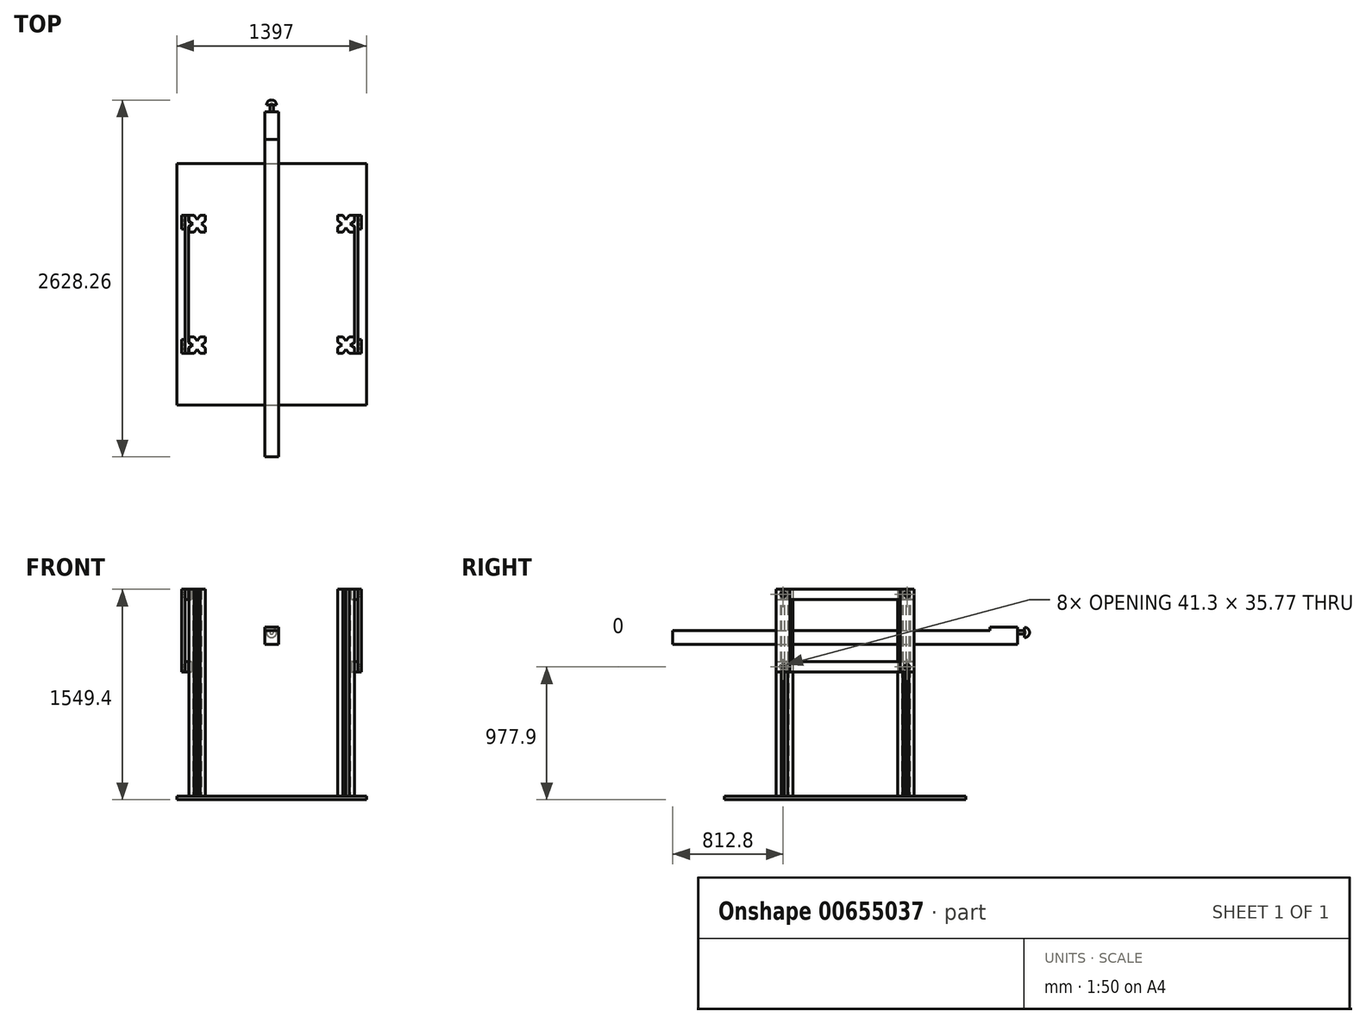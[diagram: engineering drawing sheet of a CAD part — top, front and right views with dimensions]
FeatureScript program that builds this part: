
annotation { "Feature Type Name" : "Feature", "Feature Type Description" : "" }
export const myFeature = defineFeature(function(context is Context, id is Id, definition is map)
    precondition{}
    {
        {
            var Q0;
            Q0=qCreatedBy(makeId("Top.planeOp"),FACE);
            var sketch = newSketch(context, id + "F0", { "sketchPlane" : qUnion([Q0])});
            skLineSegment(sketch, "E0.bottom", {"start": v(-698.5, 889) * mm, "end": v(698.5, 889) * mm});
            skLineSegment(sketch, "E0.top", {"start": v(-698.5, -889) * mm, "end": v(698.5, -889) * mm});
            skLineSegment(sketch, "E0.left", {"start": v(-698.5, 889) * mm, "end": v(-698.5, -889) * mm});
            skLineSegment(sketch, "E0.right", {"start": v(698.5, 889) * mm, "end": v(698.5, -889) * mm});
            skSolve(sketch);
        }
        {
            var Q0;
            Q0 = qSketchRegion(id + "F0", true);
            extrude(context, id + "F1", {"entities" : qUnion([Q0]), "depth" : 25.4 * mm, "offsetDistance" : 25.4 * mm});
        }
        {
            var Q0;
            Q0=makeQuery(id+"F1.opExtrude","CAP_FACE",FACE,{"disambiguationData":[OSD([sQuery(id+"F0.wireOp",EDGE,"E0.bottom"),sQuery(id+"F0.wireOp",EDGE,"E0.top"),sQuery(id+"F0.wireOp",EDGE,"E0.left"),sQuery(id+"F0.wireOp",EDGE,"E0.right")])],"isStart":false});
            var sketch = newSketch(context, id + "F2", { "sketchPlane" : qUnion([Q0])});
            skLineSegment(sketch, "E1", {"start": v(-609.6, 508) * mm, "end": v(-571.5, 508) * mm});
            skLineSegment(sketch, "E2", {"start": v(-571.5, 508) * mm, "end": v(-548.3, 477.77) * mm});
            skLineSegment(sketch, "E3", {"start": v(-548.3, 477.77) * mm, "end": v(-525.11, 508) * mm});
            skLineSegment(sketch, "E4", {"start": v(-525.11, 508) * mm, "end": v(-487.01, 508) * mm});
            skLineSegment(sketch, "E5", {"start": v(-487.01, 508) * mm, "end": v(-487.01, 469.9) * mm});
            skLineSegment(sketch, "E6", {"start": v(-487.01, 469.9) * mm, "end": v(-517.24, 446.7) * mm});
            skLineSegment(sketch, "E7", {"start": v(-517.24, 446.7) * mm, "end": v(-487.01, 423.51) * mm});
            skLineSegment(sketch, "E8", {"start": v(-487.01, 423.51) * mm, "end": v(-487.01, 385.41) * mm});
            skLineSegment(sketch, "E9", {"start": v(-487.01, 385.41) * mm, "end": v(-525.11, 385.41) * mm});
            skLineSegment(sketch, "E10", {"start": v(-525.11, 385.41) * mm, "end": v(-548.3, 415.64) * mm});
            skLineSegment(sketch, "E11", {"start": v(-548.3, 415.64) * mm, "end": v(-571.5, 385.41) * mm});
            skLineSegment(sketch, "E12", {"start": v(-571.5, 385.41) * mm, "end": v(-609.6, 385.41) * mm});
            skLineSegment(sketch, "E13", {"start": v(-609.6, 385.41) * mm, "end": v(-609.6, 423.51) * mm});
            skLineSegment(sketch, "E14", {"start": v(-609.6, 423.51) * mm, "end": v(-579.37, 446.7) * mm});
            skLineSegment(sketch, "E15", {"start": v(-579.37, 446.7) * mm, "end": v(-609.6, 469.9) * mm});
            skLineSegment(sketch, "E16", {"start": v(-609.6, 469.9) * mm, "end": v(-609.6, 508) * mm});
            skLineSegment(sketch, "E17.MirrorCS", {"start": v(-571.5, -508) * mm, "end": v(-548.3, -477.77) * mm});
            skLineSegment(sketch, "E18.MirrorCS", {"start": v(-548.3, -477.77) * mm, "end": v(-525.11, -508) * mm});
            skLineSegment(sketch, "E19.MirrorCS", {"start": v(-525.11, -508) * mm, "end": v(-487.01, -508) * mm});
            skLineSegment(sketch, "E20.MirrorCS", {"start": v(-487.01, -508) * mm, "end": v(-487.01, -469.9) * mm});
            skLineSegment(sketch, "E21.MirrorCS", {"start": v(-487.01, -469.9) * mm, "end": v(-517.24, -446.7) * mm});
            skLineSegment(sketch, "E22.MirrorCS", {"start": v(-517.24, -446.7) * mm, "end": v(-487.01, -423.51) * mm});
            skLineSegment(sketch, "E23.MirrorCS", {"start": v(-487.01, -423.51) * mm, "end": v(-487.01, -385.41) * mm});
            skLineSegment(sketch, "E24.MirrorCS", {"start": v(-487.01, -385.41) * mm, "end": v(-525.11, -385.41) * mm});
            skLineSegment(sketch, "E25.MirrorCS", {"start": v(-609.6, -508) * mm, "end": v(-571.5, -508) * mm});
            skLineSegment(sketch, "E26.MirrorCS", {"start": v(-571.5, -385.41) * mm, "end": v(-609.6, -385.41) * mm});
            skLineSegment(sketch, "E27.MirrorCS", {"start": v(-609.6, -385.41) * mm, "end": v(-609.6, -423.51) * mm});
            skLineSegment(sketch, "E28.MirrorCS", {"start": v(-609.6, -423.51) * mm, "end": v(-579.37, -446.7) * mm});
            skLineSegment(sketch, "E29.MirrorCS", {"start": v(-548.3, -415.64) * mm, "end": v(-571.5, -385.41) * mm});
            skLineSegment(sketch, "E30.MirrorCS", {"start": v(-525.11, -385.41) * mm, "end": v(-548.3, -415.64) * mm});
            skLineSegment(sketch, "E31.MirrorCS", {"start": v(-609.6, -469.9) * mm, "end": v(-609.6, -508) * mm});
            skLineSegment(sketch, "E32.MirrorCS", {"start": v(-579.37, -446.7) * mm, "end": v(-609.6, -469.9) * mm});
            skLineSegment(sketch, "E33.MirrorCS", {"start": v(525.11, -385.41) * mm, "end": v(548.3, -415.64) * mm});
            skLineSegment(sketch, "E34.MirrorCS", {"start": v(571.5, 385.41) * mm, "end": v(609.6, 385.41) * mm});
            skLineSegment(sketch, "E35.MirrorCS", {"start": v(525.11, -508) * mm, "end": v(487.01, -508) * mm});
            skLineSegment(sketch, "E36.MirrorCS", {"start": v(571.5, 508) * mm, "end": v(548.3, 477.77) * mm});
            skLineSegment(sketch, "E37.MirrorCS", {"start": v(517.24, 446.7) * mm, "end": v(487.01, 423.51) * mm});
            skLineSegment(sketch, "E38.MirrorCS", {"start": v(609.6, -385.41) * mm, "end": v(609.6, -423.51) * mm});
            skLineSegment(sketch, "E39.MirrorCS", {"start": v(609.6, 469.9) * mm, "end": v(609.6, 508) * mm});
            skLineSegment(sketch, "E40.MirrorCS", {"start": v(609.6, -508) * mm, "end": v(571.5, -508) * mm});
            skLineSegment(sketch, "E41.MirrorCS", {"start": v(579.37, -446.7) * mm, "end": v(609.6, -469.9) * mm});
            skLineSegment(sketch, "E42.MirrorCS", {"start": v(517.24, -446.7) * mm, "end": v(487.01, -423.51) * mm});
            skLineSegment(sketch, "E43.MirrorCS", {"start": v(487.01, 508) * mm, "end": v(487.01, 469.9) * mm});
            skLineSegment(sketch, "E44.MirrorCS", {"start": v(609.6, -469.9) * mm, "end": v(609.6, -508) * mm});
            skLineSegment(sketch, "E45.MirrorCS", {"start": v(487.01, -423.51) * mm, "end": v(487.01, -385.41) * mm});
            skLineSegment(sketch, "E46.MirrorCS", {"start": v(487.01, -469.9) * mm, "end": v(517.24, -446.7) * mm});
            skLineSegment(sketch, "E47.MirrorCS", {"start": v(487.01, 385.41) * mm, "end": v(525.11, 385.41) * mm});
            skLineSegment(sketch, "E48.MirrorCS", {"start": v(609.6, -423.51) * mm, "end": v(579.37, -446.7) * mm});
            skLineSegment(sketch, "E49.MirrorCS", {"start": v(548.3, 477.77) * mm, "end": v(525.11, 508) * mm});
            skLineSegment(sketch, "E50.MirrorCS", {"start": v(487.01, -385.41) * mm, "end": v(525.11, -385.41) * mm});
            skLineSegment(sketch, "E51.MirrorCS", {"start": v(571.5, -385.41) * mm, "end": v(609.6, -385.41) * mm});
            skLineSegment(sketch, "E52.MirrorCS", {"start": v(487.01, -508) * mm, "end": v(487.01, -469.9) * mm});
            skLineSegment(sketch, "E53.MirrorCS", {"start": v(548.3, -415.64) * mm, "end": v(571.5, -385.41) * mm});
            skLineSegment(sketch, "E54.MirrorCS", {"start": v(548.3, -477.77) * mm, "end": v(525.11, -508) * mm});
            skLineSegment(sketch, "E55.MirrorCS", {"start": v(487.01, 469.9) * mm, "end": v(517.24, 446.7) * mm});
            skLineSegment(sketch, "E56.MirrorCS", {"start": v(525.11, 385.41) * mm, "end": v(548.3, 415.64) * mm});
            skLineSegment(sketch, "E57.MirrorCS", {"start": v(548.3, 415.64) * mm, "end": v(571.5, 385.41) * mm});
            skLineSegment(sketch, "E58.MirrorCS", {"start": v(571.5, -508) * mm, "end": v(548.3, -477.77) * mm});
            skLineSegment(sketch, "E59.MirrorCS", {"start": v(487.01, 423.51) * mm, "end": v(487.01, 385.41) * mm});
            skLineSegment(sketch, "E60.MirrorCS", {"start": v(525.11, 508) * mm, "end": v(487.01, 508) * mm});
            skLineSegment(sketch, "E61.MirrorCS", {"start": v(609.6, 423.51) * mm, "end": v(579.37, 446.7) * mm});
            skLineSegment(sketch, "E62.MirrorCS", {"start": v(579.37, 446.7) * mm, "end": v(609.6, 469.9) * mm});
            skLineSegment(sketch, "E63.MirrorCS", {"start": v(609.6, 508) * mm, "end": v(571.5, 508) * mm});
            skLineSegment(sketch, "E64.MirrorCS", {"start": v(609.6, 385.41) * mm, "end": v(609.6, 423.51) * mm});
            skSolve(sketch);
        }
        {
            var Q0;
            Q0 = qSketchRegion(id + "F2", true);
            extrude(context, id + "F3", {"entities" : qUnion([Q0]), "operationType" : NewBodyOperationType.ADD, "depth" : 1524 * mm, "offsetDistance" : 25.4 * mm});
        }
        {
            var Q0;
            Q0=qCreatedBy(makeId("Front.planeOp"),FACE);
            var sketch = newSketch(context, id + "F4", { "sketchPlane" : qUnion([Q0])});
            skLineSegment(sketch, "E65.bottom", {"start": v(-50.8, 1244.6) * mm, "end": v(50.8, 1244.6) * mm});
            skLineSegment(sketch, "E65.top", {"start": v(-50.8, 1143) * mm, "end": v(50.8, 1143) * mm});
            skLineSegment(sketch, "E65.left", {"start": v(-50.8, 1244.6) * mm, "end": v(-50.8, 1143) * mm});
            skLineSegment(sketch, "E65.right", {"start": v(50.8, 1244.6) * mm, "end": v(50.8, 1143) * mm});
            skSolve(sketch);
        }
        {
            var Q0;
            Q0 = qSketchRegion(id + "F4", true);
            extrude(context, id + "F5", {"entities" : qUnion([Q0]), "endBound" : BoundingType.SYMMETRIC, "depth" : 2540 * mm, "offsetDistance" : 25.4 * mm});
        }
        {
            var Q0;
            Q0=makeQuery(id+"F5.opExtrude","SWEPT_FACE",FACE,{"disambiguationData":[OSD([sQuery(id+"F4.wireOp",EDGE,"E65.bottom")])]});
            var sketch = newSketch(context, id + "F6", { "sketchPlane" : qUnion([Q0])});
            skLineSegment(sketch, "E66.bottom", {"start": v(-50.8, 1270) * mm, "end": v(50.8, 1270) * mm});
            skLineSegment(sketch, "E66.top", {"start": v(-50.8, 1066.8) * mm, "end": v(50.8, 1066.8) * mm});
            skLineSegment(sketch, "E66.left", {"start": v(-50.8, 1270) * mm, "end": v(-50.8, 1066.8) * mm});
            skLineSegment(sketch, "E66.right", {"start": v(50.8, 1270) * mm, "end": v(50.8, 1066.8) * mm});
            skSolve(sketch);
        }
        {
            var Q0;
            Q0 = qSketchRegion(id + "F6", true);
            extrude(context, id + "F7", {"entities" : qUnion([Q0]), "operationType" : NewBodyOperationType.ADD, "depth" : 25.4 * mm, "offsetDistance" : 25.4 * mm});
        }
        {
            var Q0;
            Q0=makeQuery(id+"F7.boolean.opBoolean","MERGE",FACE,{"derivedFrom":[makeQuery(id+"F5.opExtrude","CAP_FACE",FACE,{"disambiguationData":[OSD([sQuery(id+"F4.wireOp",EDGE,"E65.bottom"),sQuery(id+"F4.wireOp",EDGE,"E65.top"),sQuery(id+"F4.wireOp",EDGE,"E65.left"),sQuery(id+"F4.wireOp",EDGE,"E65.right")])],"isStart":true}),makeQuery(id+"F7.opExtrude","SWEPT_FACE",FACE,{"disambiguationData":[OSD([sQuery(id+"F6.wireOp",EDGE,"E66.bottom")])]})]});
            var sketch = newSketch(context, id + "F8", { "sketchPlane" : qUnion([Q0])});
            skCircle(sketch, "E67", {"center": v(0, 1231.9) * mm, "radius": 12.7 * mm});
            skSolve(sketch);
        }
        {
            var Q0;
            Q0 = qSketchRegion(id + "F8", true);
            extrude(context, id + "F9", {"entities" : qUnion([Q0]), "operationType" : NewBodyOperationType.ADD, "depth" : 50.8 * mm, "offsetDistance" : 25.4 * mm});
        }
        {
            var Q0;
            Q0=makeQuery(id+"F9.opExtrude","CAP_FACE",FACE,{"disambiguationData":[OSD([sQuery(id+"F8.wireOp",EDGE,"E67")])],"isStart":false});
            var sketch = newSketch(context, id + "F10", { "sketchPlane" : qUnion([Q0])});
            skLineSegment(sketch, "E68", {"start": v(-37.47, 1231.9) * mm, "end": v(37.46, 1231.9) * mm});
            skArc(sketch, "E69", {"start": v(-37.47, 1231.9) * mm, "mid": v(0, 1194.43) * mm, "end": v(37.46, 1231.9) * mm});
            skSolve(sketch);
        }
        {
            var Q0;
            {var subQ0=sQuery(id+"F10.wireOp",EDGE,"E69");Q0=makeQuery(id+"F10.imprint","IMPRINT",FACE,{"disambiguationData":[TD([[makeQuery(id+"F10.imprint","IMPRINT",EDGE,{"derivedFrom":subQ0}),1.0]])]});}
            var Q1;
            Q1=sQuery(id+"F10.wireOp",EDGE,"E68");
            revolve(context, id + "F11", {"operationType" : NewBodyOperationType.ADD, "entities" : qUnion([Q0]), "axis" : qUnion([Q1]), "revolveType" : RevolveType.ONE_DIRECTION, "oppositeDirection" : true, "angle" : 180 * degree});
        }
        {
            var Q0;
            Q0=makeQuery(id+"F3.opExtrude","CAP_FACE",FACE,{"disambiguationData":[OSD([sQuery(id+"F2.wireOp",EDGE,"E45.MirrorCS"),sQuery(id+"F2.wireOp",EDGE,"E44.MirrorCS"),sQuery(id+"F2.wireOp",EDGE,"E42.MirrorCS"),sQuery(id+"F2.wireOp",EDGE,"E41.MirrorCS"),sQuery(id+"F2.wireOp",EDGE,"E46.MirrorCS"),sQuery(id+"F2.wireOp",EDGE,"E48.MirrorCS"),sQuery(id+"F2.wireOp",EDGE,"E50.MirrorCS"),sQuery(id+"F2.wireOp",EDGE,"E51.MirrorCS"),sQuery(id+"F2.wireOp",EDGE,"E52.MirrorCS"),sQuery(id+"F2.wireOp",EDGE,"E38.MirrorCS"),sQuery(id+"F2.wireOp",EDGE,"E33.MirrorCS"),sQuery(id+"F2.wireOp",EDGE,"E58.MirrorCS"),sQuery(id+"F2.wireOp",EDGE,"E40.MirrorCS"),sQuery(id+"F2.wireOp",EDGE,"E54.MirrorCS"),sQuery(id+"F2.wireOp",EDGE,"E53.MirrorCS"),sQuery(id+"F2.wireOp",EDGE,"E35.MirrorCS")])],"isStart":false});
            var sketch = newSketch(context, id + "F12", { "sketchPlane" : qUnion([Q0])});
            skLineSegment(sketch, "E70.bottom", {"start": v(637.54, 508) * mm, "end": v(612.14, 508) * mm});
            skLineSegment(sketch, "E70.top", {"start": v(637.54, -508) * mm, "end": v(612.14, -508) * mm});
            skLineSegment(sketch, "E70.left", {"start": v(637.54, 508) * mm, "end": v(637.54, -508) * mm});
            skLineSegment(sketch, "E71", {"start": v(612.14, -508) * mm, "end": v(612.14, -464.82) * mm});
            skLineSegment(sketch, "E72", {"start": v(612.14, -464.82) * mm, "end": v(587.96, -446.26) * mm});
            skLineSegment(sketch, "E73", {"start": v(587.96, -446.26) * mm, "end": v(612.14, -427.7) * mm});
            skLineSegment(sketch, "E74", {"start": v(612.14, -427.7) * mm, "end": v(612.14, 427.7) * mm});
            skLineSegment(sketch, "E75", {"start": v(612.14, 427.7) * mm, "end": v(587.96, 446.26) * mm});
            skLineSegment(sketch, "E76", {"start": v(587.96, 446.26) * mm, "end": v(612.14, 464.82) * mm});
            skLineSegment(sketch, "E77", {"start": v(612.14, 464.82) * mm, "end": v(612.14, 508) * mm});
            skLineSegment(sketch, "E78.MirrorCS", {"start": v(-637.54, 508) * mm, "end": v(-612.14, 508) * mm});
            skLineSegment(sketch, "E79.MirrorCS", {"start": v(-637.54, -508) * mm, "end": v(-612.14, -508) * mm});
            skLineSegment(sketch, "E80.MirrorCS", {"start": v(-612.14, -508) * mm, "end": v(-612.14, -464.82) * mm});
            skLineSegment(sketch, "E81.MirrorCS", {"start": v(-612.14, 427.7) * mm, "end": v(-587.96, 446.26) * mm});
            skLineSegment(sketch, "E82.MirrorCS", {"start": v(-587.96, 446.26) * mm, "end": v(-612.14, 464.82) * mm});
            skLineSegment(sketch, "E83.MirrorCS", {"start": v(-587.96, -446.26) * mm, "end": v(-612.14, -427.7) * mm});
            skLineSegment(sketch, "E84.MirrorCS", {"start": v(-612.14, -464.82) * mm, "end": v(-587.96, -446.26) * mm});
            skLineSegment(sketch, "E85.MirrorCS", {"start": v(-612.14, 464.82) * mm, "end": v(-612.14, 508) * mm});
            skLineSegment(sketch, "E86.MirrorCS", {"start": v(-637.54, 508) * mm, "end": v(-637.54, -508) * mm});
            skLineSegment(sketch, "E87.MirrorCS", {"start": v(-612.14, -427.7) * mm, "end": v(-612.14, 427.7) * mm});
            skSolve(sketch);
        }
        {
            var Q0;
            Q0 = qSketchRegion(id + "F12", true);
            extrude(context, id + "F13", {"entities" : qUnion([Q0]), "oppositeDirection" : true, "depth" : 76.2 * mm, "offsetDistance" : 25.4 * mm});
        }
        {
            var Q0;
            Q0=makeQuery(id+"F13.opExtrude","SWEPT_BODY",BODY,{"disambiguationData":[OSD([sQuery(id+"F12.wireOp",EDGE,"E70.bottom"),sQuery(id+"F12.wireOp",EDGE,"E70.top"),sQuery(id+"F12.wireOp",EDGE,"E70.left"),sQuery(id+"F12.wireOp",EDGE,"E71"),sQuery(id+"F12.wireOp",EDGE,"E72"),sQuery(id+"F12.wireOp",EDGE,"E73"),sQuery(id+"F12.wireOp",EDGE,"E74"),sQuery(id+"F12.wireOp",EDGE,"E75"),sQuery(id+"F12.wireOp",EDGE,"E76"),sQuery(id+"F12.wireOp",EDGE,"E77")])]});
            var Q1;
            Q1=makeQuery(id+"F13.opExtrude","SWEPT_BODY",BODY,{"disambiguationData":[OSD([sQuery(id+"F12.wireOp",EDGE,"E78.MirrorCS"),sQuery(id+"F12.wireOp",EDGE,"E79.MirrorCS"),sQuery(id+"F12.wireOp",EDGE,"E80.MirrorCS"),sQuery(id+"F12.wireOp",EDGE,"E81.MirrorCS"),sQuery(id+"F12.wireOp",EDGE,"E82.MirrorCS"),sQuery(id+"F12.wireOp",EDGE,"E83.MirrorCS"),sQuery(id+"F12.wireOp",EDGE,"E84.MirrorCS"),sQuery(id+"F12.wireOp",EDGE,"E85.MirrorCS"),sQuery(id+"F12.wireOp",EDGE,"E86.MirrorCS"),sQuery(id+"F12.wireOp",EDGE,"E87.MirrorCS")])]});
            var Q2;
            Q2=makeQuery(id+"F5.opExtrude","SWEPT_FACE",FACE,{"disambiguationData":[OSD([sQuery(id+"F4.wireOp",EDGE,"E65.bottom")])]});
            mirror(context, id + "F14", {"entities" : qUnion([Q0, Q1]), "mirrorPlane" : qUnion([Q2])});
        }
        {
            var Q0;
            Q0=makeQuery(id+"F13.opExtrude","SWEPT_FACE",FACE,{"disambiguationData":[OSD([sQuery(id+"F12.wireOp",EDGE,"E70.left")])]});
            var sketch = newSketch(context, id + "F15", { "sketchPlane" : qUnion([Q0])});
            skLineSegment(sketch, "E88.bottom", {"start": v(508, 1549.4) * mm, "end": v(406.4, 1549.4) * mm});
            skLineSegment(sketch, "E88.top", {"start": v(508, 939.8) * mm, "end": v(406.4, 939.8) * mm});
            skLineSegment(sketch, "E88.left", {"start": v(508, 1549.4) * mm, "end": v(508, 939.8) * mm});
            skLineSegment(sketch, "E88.right", {"start": v(406.4, 1549.4) * mm, "end": v(406.4, 939.8) * mm});
            skCircle(sketch, "E89.cCircle", {"center": v(457.2, 1511.3) * mm, "radius": 17.88 * mm, "construction": true});
            skLineSegment(sketch, "E89.0", {"start": v(436.55, 1511.3) * mm, "end": v(446.88, 1529.18) * mm});
            skLineSegment(sketch, "E89.1", {"start": v(446.88, 1529.18) * mm, "end": v(467.52, 1529.18) * mm});
            skLineSegment(sketch, "E89.2", {"start": v(467.52, 1529.18) * mm, "end": v(477.85, 1511.3) * mm});
            skLineSegment(sketch, "E89.3", {"start": v(477.85, 1511.3) * mm, "end": v(467.52, 1493.42) * mm});
            skLineSegment(sketch, "E89.4", {"start": v(467.52, 1493.42) * mm, "end": v(446.88, 1493.42) * mm});
            skLineSegment(sketch, "E89.5", {"start": v(446.88, 1493.42) * mm, "end": v(436.55, 1511.3) * mm});
            skPoint(sketch, "E89.0.midPoint", {"position": v(441.71, 1520.24) * mm});
            skCircle(sketch, "E90.cCircle", {"center": v(457.2, 977.9) * mm, "radius": 17.88 * mm, "construction": true});
            skLineSegment(sketch, "E90.0", {"start": v(436.55, 977.9) * mm, "end": v(446.88, 995.78) * mm});
            skLineSegment(sketch, "E90.1", {"start": v(446.88, 995.78) * mm, "end": v(467.52, 995.78) * mm});
            skLineSegment(sketch, "E90.2", {"start": v(467.52, 995.78) * mm, "end": v(477.85, 977.9) * mm});
            skLineSegment(sketch, "E90.3", {"start": v(477.85, 977.9) * mm, "end": v(467.52, 960.02) * mm});
            skLineSegment(sketch, "E90.4", {"start": v(467.52, 960.02) * mm, "end": v(446.88, 960.02) * mm});
            skLineSegment(sketch, "E90.5", {"start": v(446.88, 960.02) * mm, "end": v(436.55, 977.9) * mm});
            skPoint(sketch, "E90.0.midPoint", {"position": v(441.71, 986.84) * mm});
            skLineSegment(sketch, "E91.MirrorCS", {"start": v(-446.88, 960.02) * mm, "end": v(-436.55, 977.9) * mm});
            skLineSegment(sketch, "E92.MirrorCS", {"start": v(-467.52, 1529.18) * mm, "end": v(-477.85, 1511.3) * mm});
            skLineSegment(sketch, "E93.MirrorCS", {"start": v(-446.88, 1529.18) * mm, "end": v(-467.52, 1529.18) * mm});
            skLineSegment(sketch, "E94.MirrorCS", {"start": v(-436.55, 1511.3) * mm, "end": v(-446.88, 1529.18) * mm});
            skLineSegment(sketch, "E95.MirrorCS", {"start": v(-467.52, 995.78) * mm, "end": v(-477.85, 977.9) * mm});
            skLineSegment(sketch, "E96.MirrorCS", {"start": v(-446.88, 995.78) * mm, "end": v(-467.52, 995.78) * mm});
            skLineSegment(sketch, "E97.MirrorCS", {"start": v(-436.55, 977.9) * mm, "end": v(-446.88, 995.78) * mm});
            skCircle(sketch, "E98.MirrorC", {"center": v(-457.2, 977.9) * mm, "radius": 17.88 * mm, "construction": true});
            skLineSegment(sketch, "E99.MirrorCS", {"start": v(-446.88, 1493.42) * mm, "end": v(-436.55, 1511.3) * mm});
            skLineSegment(sketch, "E100.MirrorCS", {"start": v(-467.52, 1493.42) * mm, "end": v(-446.88, 1493.42) * mm});
            skLineSegment(sketch, "E101.MirrorCS", {"start": v(-477.85, 1511.3) * mm, "end": v(-467.52, 1493.42) * mm});
            skLineSegment(sketch, "E102.MirrorCS", {"start": v(-467.52, 960.02) * mm, "end": v(-446.88, 960.02) * mm});
            skLineSegment(sketch, "E103.MirrorCS", {"start": v(-477.85, 977.9) * mm, "end": v(-467.52, 960.02) * mm});
            skCircle(sketch, "E104.MirrorC", {"center": v(-457.2, 1511.3) * mm, "radius": 17.88 * mm, "construction": true});
            skLineSegment(sketch, "E105.MirrorCS", {"start": v(-508, 1549.4) * mm, "end": v(-406.4, 1549.4) * mm});
            skLineSegment(sketch, "E106.MirrorCS", {"start": v(-508, 939.8) * mm, "end": v(-406.4, 939.8) * mm});
            skPoint(sketch, "E107.MirrorP", {"position": v(-441.71, 1520.24) * mm});
            skPoint(sketch, "E108.MirrorP", {"position": v(-441.71, 986.84) * mm});
            skLineSegment(sketch, "E109.MirrorCS", {"start": v(-406.4, 1549.4) * mm, "end": v(-406.4, 939.8) * mm});
            skLineSegment(sketch, "E110.MirrorCS", {"start": v(-508, 1549.4) * mm, "end": v(-508, 939.8) * mm});
            skSolve(sketch);
        }
        {
            var Q0;
            Q0 = qSketchRegion(id + "F15", true);
            extrude(context, id + "F16", {"entities" : qUnion([Q0]), "depth" : 25.4 * mm, "offsetDistance" : 25.4 * mm});
        }
        {
            var Q0;
            Q0=makeQuery(id+"F16.opExtrude","SWEPT_BODY",BODY,{"disambiguationData":[OSD([sQuery(id+"F15.wireOp",EDGE,"E91.MirrorCS"),sQuery(id+"F15.wireOp",EDGE,"E92.MirrorCS"),sQuery(id+"F15.wireOp",EDGE,"E93.MirrorCS"),sQuery(id+"F15.wireOp",EDGE,"E94.MirrorCS"),sQuery(id+"F15.wireOp",EDGE,"E95.MirrorCS"),sQuery(id+"F15.wireOp",EDGE,"E96.MirrorCS"),sQuery(id+"F15.wireOp",EDGE,"E97.MirrorCS"),sQuery(id+"F15.wireOp",EDGE,"E99.MirrorCS"),sQuery(id+"F15.wireOp",EDGE,"E100.MirrorCS"),sQuery(id+"F15.wireOp",EDGE,"E101.MirrorCS"),sQuery(id+"F15.wireOp",EDGE,"E102.MirrorCS"),sQuery(id+"F15.wireOp",EDGE,"E103.MirrorCS"),sQuery(id+"F15.wireOp",EDGE,"E105.MirrorCS"),sQuery(id+"F15.wireOp",EDGE,"E106.MirrorCS"),sQuery(id+"F15.wireOp",EDGE,"E109.MirrorCS"),sQuery(id+"F15.wireOp",EDGE,"E110.MirrorCS")])]});
            var Q1;
            Q1=makeQuery(id+"F16.opExtrude","SWEPT_BODY",BODY,{"disambiguationData":[OSD([sQuery(id+"F15.wireOp",EDGE,"E88.bottom"),sQuery(id+"F15.wireOp",EDGE,"E88.top"),sQuery(id+"F15.wireOp",EDGE,"E88.left"),sQuery(id+"F15.wireOp",EDGE,"E88.right"),sQuery(id+"F15.wireOp",EDGE,"E89.0"),sQuery(id+"F15.wireOp",EDGE,"E89.1"),sQuery(id+"F15.wireOp",EDGE,"E89.2"),sQuery(id+"F15.wireOp",EDGE,"E89.3"),sQuery(id+"F15.wireOp",EDGE,"E89.4"),sQuery(id+"F15.wireOp",EDGE,"E89.5"),sQuery(id+"F15.wireOp",EDGE,"E90.0"),sQuery(id+"F15.wireOp",EDGE,"E90.1"),sQuery(id+"F15.wireOp",EDGE,"E90.2"),sQuery(id+"F15.wireOp",EDGE,"E90.3"),sQuery(id+"F15.wireOp",EDGE,"E90.4"),sQuery(id+"F15.wireOp",EDGE,"E90.5")])]});
            var Q2;
            Q2=qCreatedBy(makeId("Right.planeOp"),FACE);
            mirror(context, id + "F17", {"entities" : qUnion([Q0, Q1]), "mirrorPlane" : qUnion([Q2])});
        }
    });
